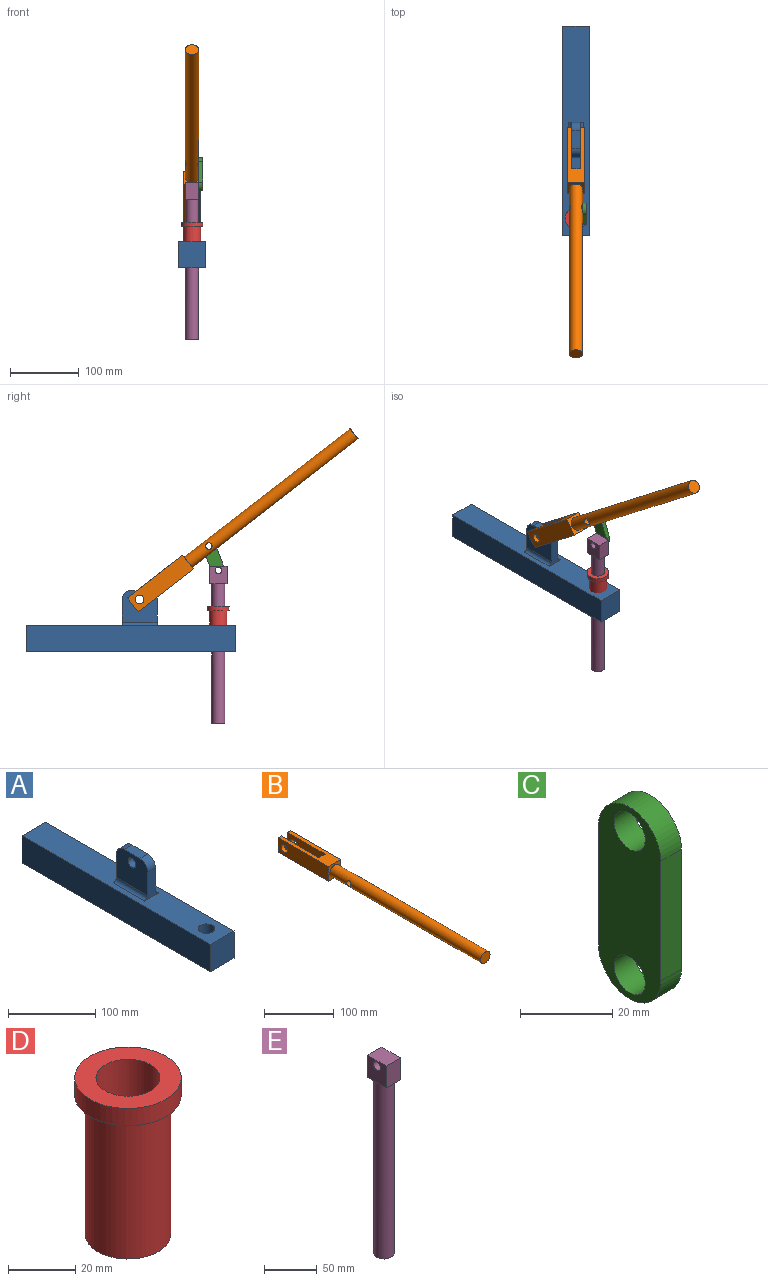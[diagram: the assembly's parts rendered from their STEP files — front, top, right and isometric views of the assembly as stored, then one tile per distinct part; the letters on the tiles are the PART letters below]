
ASSEMBLY  parts=5 mates=5
PART A: 17 faces, bbox 38.1x304.8x88.9 mm
  f0: plane 304.8x38.1mm, normal (0,0,1), area 10173.5mm2, adj f1,f2,f3,f4,f6,f8,f10,f12
  f1: plane 304.8x38.1mm, normal (1,0,0), area 11612.9mm2, adj f0,f2,f4,f5
  f2: plane 38.1x38.1mm, normal (0,1,0), area 1451.6mm2, adj f0,f1,f3,f5
  f3: plane 304.8x38.1mm, normal (-1,0,0), area 11612.9mm2, adj f0,f2,f4,f5
  f4: plane 38.1x38.1mm, normal (0,-1,0), area 1451.6mm2, adj f0,f1,f3,f5
  f5: plane 304.8x38.1mm, normal (0,0,-1), area 11334.8mm2, adj f1,f2,f3,f4,f6
  f6: cylinder r=9.41mm len=38.1mm, axis (0,0,1), area 2252.3mm2, adj f0,f5
  f7: plane 50.8x45.72mm, normal (1,0,0), area 2126.7mm2, adj f8,f10,f11,f13,f14,f15,f16
  f8: plane 38.1x22.86mm, normal (0,1,0), area 494.9mm2, adj f0,f7,f9,f12,f13,f15
  f9: plane 50.8x45.72mm, normal (-1,0,0), area 2126.7mm2, adj f8,f10,f11,f12,f14,f15,f16
  f10: plane 38.1x22.86mm, normal (0,-1,0), area 494.9mm2, adj f0,f7,f9,f12,f13,f16
  f11: plane 25.4x12.7mm, normal (0,0,1), area 322.6mm2, adj f7,f9,f15,f16
  f12: cylinder r=5.08mm len=50.8mm, axis (0,-1,0), area 405.4mm2, adj f0,f8,f9,f10
  f13: cylinder r=5.08mm len=50.8mm, axis (0,1,0), area 405.4mm2, adj f0,f7,f8,f10
  f14: cylinder r=6.35mm len=12.7mm, axis (1,0,0), area 506.7mm2, adj f7,f9
  f15: cylinder r=12.7mm len=12.7mm, axis (1,0,0), area 253.4mm2, adj f7,f8,f9,f11
  f16: cylinder r=12.7mm len=12.7mm, axis (-1,0,0), area 253.4mm2, adj f7,f9,f10,f11
PART B: 15 faces, bbox 25.4x406.4x25.4 mm
  f0: plane 25.4x6.35mm, normal (0,1,0), area 161.3mm2, adj f1,f2,f3,f7
  f1: plane 101.6x25.4mm, normal (0,0,1), area 1612.9mm2, adj f0,f3,f4,f5,f6,f7,f8,f9
  f2: plane 101.6x25.4mm, normal (0,0,-1), area 1612.9mm2, adj f0,f3,f4,f5,f6,f7,f8,f9
  f3: plane 101.6x25.4mm, normal (1,0,0), area 2454mm2, adj f0,f1,f2,f6,f11
  f4: plane 25.4x6.35mm, normal (0,1,0), area 161.3mm2, adj f1,f2,f5,f8
  f5: plane 101.6x25.4mm, normal (-1,0,0), area 2454mm2, adj f1,f2,f4,f6,f10
  f6: plane 25.4x25.4mm, normal (0,-1,0), area 360.1mm2, adj f1,f2,f3,f5,f12
  f7: plane 76.2x25.4mm, normal (-1,0,0), area 1808.8mm2, adj f0,f1,f2,f9,f11
  f8: plane 76.2x25.4mm, normal (1,0,0), area 1808.8mm2, adj f1,f2,f4,f9,f10
  f9: plane 25.4x12.7mm, normal (0,1,0), area 322.6mm2, adj f1,f2,f7,f8
  f10: cylinder r=6.35mm len=12.7mm, axis (1,0,0), area 253.4mm2, adj f5,f8
  f11: cylinder r=6.35mm len=12.7mm, axis (1,0,0), area 253.4mm2, adj f3,f7
  f12: cylinder r=9.53mm len=304.8mm, axis (0,1,0), area 18093.9mm2, adj f6,f13,f14
  f13: plane 19.05x19.05mm, normal (0,-1,0), area 285mm2, adj f12
  f14: cylinder r=4.76mm len=19.05mm, axis (1,0,0), area 532.5mm2, adj f12
PART C: 8 faces, bbox 6.4x19.1x50.8 mm
  f0: plane 31.75x6.35mm, normal (0,1,0), area 201.6mm2, adj f4,f5,f6,f7
  f1: plane 31.75x6.35mm, normal (0,-1,0), area 201.6mm2, adj f4,f5,f6,f7
  f2: cylinder r=4.76mm len=9.53mm, axis (-1,0,0), area 190mm2, adj f4,f5
  f3: cylinder r=4.76mm len=9.53mm, axis (-1,0,0), area 190mm2, adj f4,f5
  f4: plane 50.8x19.05mm, normal (1,0,0), area 747.3mm2, adj f0,f1,f2,f3,f6,f7
  f5: plane 50.8x19.05mm, normal (-1,0,0), area 747.3mm2, adj f0,f1,f2,f3,f6,f7
  f6: cylinder r=9.53mm len=19.05mm, axis (-1,0,0), area 190mm2, adj f0,f1,f4,f5
  f7: cylinder r=9.53mm len=19.05mm, axis (-1,0,0), area 190mm2, adj f0,f1,f4,f5
PART D: 6 faces, bbox 31.8x31.8x57.2 mm
  f0: cylinder r=15.88mm len=31.75mm, axis (0,0,-1), area 633.4mm2, adj f3,f4
  f1: plane 25.4x25.4mm, normal (0,0,-1), area 221.7mm2, adj f2,f5
  f2: cylinder r=9.53mm len=57.15mm, axis (0,0,-1), area 3420.3mm2, adj f1,f3
  f3: plane 31.75x31.75mm, normal (0,0,1), area 506.7mm2, adj f0,f2
  f4: plane 31.75x31.75mm, normal (0,0,-1), area 285mm2, adj f0,f5
  f5: cylinder r=12.7mm len=50.8mm, axis (0,0,-1), area 4053.7mm2, adj f1,f4
PART E: 10 faces, bbox 19.1x25.4x228.6 mm
  f0: cylinder r=9.53mm len=203.2mm, axis (0,0,-1), area 12161mm2, adj f1,f2,f3
  f1: plane 19.05x19.05mm, normal (0,0,-1), area 285mm2, adj f0
  f2: plane 19.05x12.7mm, normal (0,0,-1), area 99.4mm2, adj f0,f4,f5,f6
  f3: plane 19.05x12.7mm, normal (0,0,-1), area 99.4mm2, adj f0,f4,f6,f7
  f4: plane 25.4x25.4mm, normal (1,0,0), area 573.9mm2, adj f2,f3,f5,f7,f8,f9
  f5: plane 25.4x19.05mm, normal (0,1,0), area 483.9mm2, adj f2,f4,f6,f8
  f6: plane 25.4x25.4mm, normal (-1,0,0), area 573.9mm2, adj f2,f3,f5,f7,f8,f9
  f7: plane 25.4x19.05mm, normal (0,-1,0), area 483.9mm2, adj f3,f4,f6,f8
  f8: plane 25.4x19.05mm, normal (0,0,1), area 483.9mm2, adj f4,f5,f6,f7
  f9: cylinder r=4.76mm len=19.05mm, axis (1,0,0), area 570mm2, adj f4,f6
PLACE A t=(-29.69,3.64,12.12)mm fixed
PLACE B rot(axis=(-1,0,0),37.7deg) t=(-29.69,-46.97,101.58)mm
PLACE C rot(axis=(-1,0,0),21.3deg) t=(-20.16,-116.45,148.25)mm
PLACE D rot(axis=(0,0,-1),90deg) t=(-29.69,-123.36,21.27)mm
PLACE E t=(-29.69,-123.36,-91.75)mm
MATE revolute B.f10 <-> A.f14  axis (-1,0,0) through (-23.34,-9.06,88.32)mm
MATE cylindrical D.f2 <-> A.f6  axis (0,0,-1) through (-29.69,-123.36,21.27)mm
MATE revolute C.f3 <-> E.f9  axis (-1,0,0) through (-20.16,-123.36,130.5)mm
MATE slider D.f2 <-> E.f0  axis (0,0,-1) through (-29.69,-123.36,78.42)mm
MATE cylindrical C.f2 <-> B.f14  axis (-1,0,0) through (-20.16,-109.53,166)mm
